# Revit family: Varmax 390-450
name_source: partatom
category: Mechanical Equipment
revit_build: Autodesk Revit 2014 (Build: 20130308_1515(x64)
units: mm (PartAtom-declared; Revit-internal decimal feet)

## types (2) — shared parameters
Alt. conec. = 1874 mm  [stored 6.14829 ft]
Alt. derivación gas = 1578 mm
Alt. entrada de aire = 1933 mm  [stored 6.34186 ft]
Alt. entrada/salida retorno = 1402 mm  [stored 4.59974 ft]
Altura = 2023 mm  [stored 6.63714 ft]
Ancho = 912 mm  [stored 2.99213 ft]
Assembly Code = D3020100
Conector = 168 mm  [stored 0.551181 ft]
Configuración = 2 y 3 tomas
Derivacion de gas = 38 mm
Derivacion gas = 51 mm
Derivación de vaciado = 25 mm  [stored 0.082021 ft]
Derivación salida / retorno = 51 mm
Empresa creadora del BIM = ACAE
Entrada de aire = 180 mm  [stored 0.590551 ft]
Manufacturer = Atlantic
Mínimo = 45 mm
Peso en vacío = 580 kg
Presión máxima de servicio = 6 bar
Profundidad Total = 1392 mm  [stored 4.56693 ft]
Rendimiento mínimo al 100% de potencia (80/60 ºC) = 97,8%
Rendimiento mínimo al 30% de carga (50/30 ºC) = 108,9%
Salida de humos = 200 mm  [stored 0.656168 ft]
Tipo de combustible = Gas natural (G20), en opción Gas propano (G31) hasta 320 kW
URL = http://www.ygnis.es
Volumen de agua = 287 L

## per-type parameters (varying)
| type | Caudal de gas a Pn (15 ºC) | Consumo eléctrico máximo | Description | Model | Potencia útil (50/30 ºC) |
| Varmax 390 - Caldera de pie de condensación a gas 414 kW y 6 bar (2/3 tomas) | 41,3 m3/h | 480 W | Unidad térmica de condensación para gas natural Ygnis modelo Varmax 390,  potencia útil (50/30 ºC) de 414 kW. Fabricada en acero inoxidable de alta calidad AISI 316 L. Quemador modulante desde el 20% de la potencia. Rendimiento hasta el 108 %. Clase 5 de NOx. Dimensiones (Altura x Ancho x Largo): 2067 x 897 x 1367 mm. Peso en vacío: 580 kg. Presión máxima de servicio: 6 bar. Configuración a 2 y 3 tomas.
en acero inoxidable con potencias comprendidas entre
127 y 478kW. | Varmax 390 | 414 kW |
| Varmax 450 - Caldera de pie de condensación a gas 477 kW y 6 bar (2/3 tomas) | 47,6 m3/h | 660 W | Unidad térmica de condensación para gas natural Ygnis modelo Varmax 450,  potencia útil (50/30 ºC) de 477 kW. Fabricada en acero inoxidable de alta calidad AISI 316 L. Quemador modulante desde el 20% de la potencia. Rendimiento hasta el 108 %. Clase 5 de NOx. Dimensiones (Altura x Ancho x Largo): 2067 x 897 x 1367 mm. Peso en vacío: 580 kg. Presión máxima de servicio: 6 bar. Configuración a 2 y 3 tomas.
en acero inoxidable con potencias comprendidas entre
127 y 478kW. | Varmax 450 | 477 kW |

note: [stored X ft] marks values corroborated as IEEE doubles in the binary element streams (Revit-internal decimal feet)

## geometry (parser evidence)
native form markers: Sweep x1
no freeform markers — native parametric forms only
